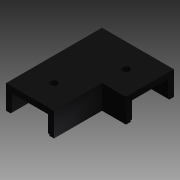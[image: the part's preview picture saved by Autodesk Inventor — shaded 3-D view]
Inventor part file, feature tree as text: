
AUTODESK INVENTOR PART (.ipt)
format: ipt  version: 2015 (Build 190159000, 159)  size: 146,432 bytes
history: native  units: in
note: dims shown in document units (in); Inventor stores cm internally (conversion verified against a paired STEP export)
features: extrude x5, sketch x5, other x2, split x1
ambient origin geometry x8: Origin, YZ Plane, XZ Plane, XY Plane, X Axis, Y Axis, Z Axis, Center Point
bodies: Solid1 (feature_tree)
feature tree (13):
  extrude  "Extrusion1"  Depth=1.0in
  extrude  "Extrusion2"  Depth=0.5in TaperAngle=0.0deg
  extrude  "Extrusion4"  Depth=0.75in
  extrude  "Extrusion5"  Depth=0.75in
  extrude  "Extrusion6"  Depth=0.03in TaperAngle=0.0deg
  split  "Split2"
  other  "Lip4"
  other  "Lip5"
  sketch  "Sketch1"  dims[d0=1.0in d1=1.0in]
  sketch  "Sketch2"  dims[d2=2.0in d3=0.0in d4=0.5in d5=0.0in]
  sketch  "Sketch5"  dims[d8=0.75in d9=0.75in]
  sketch  "Sketch6"  dims[d10=1.75in d11=0.0in d12=0.75in]
  sketch  "Sketch7"  dims[d13=0.75in d14=1.75in d15=0.0in d34=0.141in d35=1.0in d36=0.0in d38=0.03in d39=0.03in d40=0.0in d41=0.0in d42=0.0in d43=0.0in d44=0.03in d45=0.03in d46=0.0in d47=0.0in d48=0.0in d49=0.0in]
